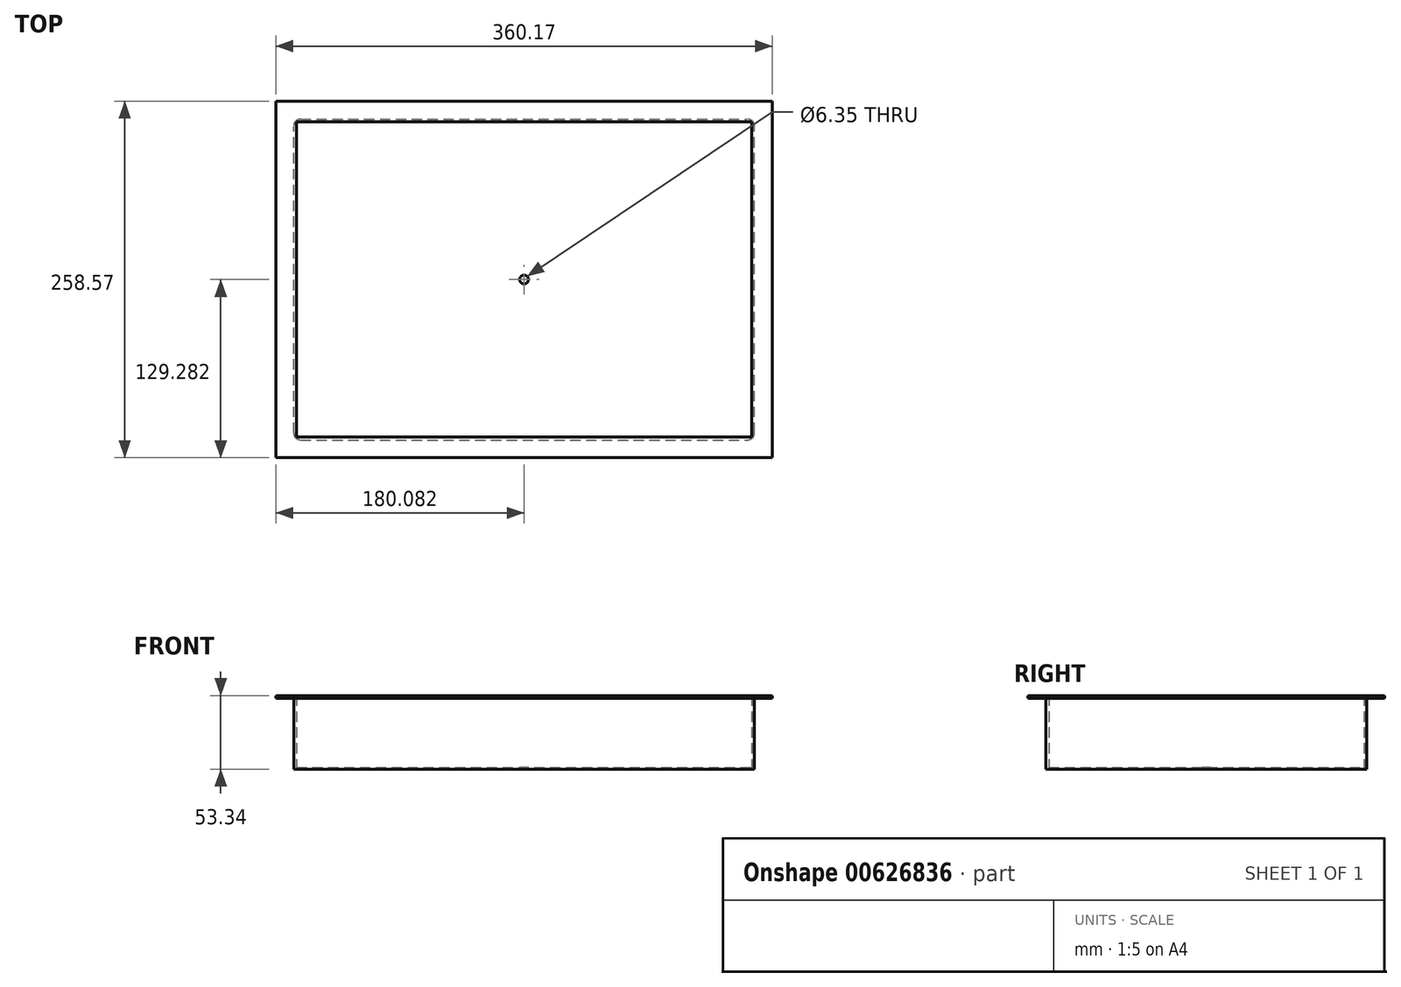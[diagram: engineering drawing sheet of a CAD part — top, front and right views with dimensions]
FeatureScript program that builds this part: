
annotation { "Feature Type Name" : "Feature", "Feature Type Description" : "" }
export const myFeature = defineFeature(function(context is Context, id is Id, definition is map)
    precondition{}
    {
        {
            var Q0;
            Q0=qCreatedBy(makeId("Top.planeOp"),FACE);
            var sketch = newSketch(context, id + "F0", { "sketchPlane" : qUnion([Q0])});
            skLineSegment(sketch, "E0.bottom", {"start": v(0, 0) * mm, "end": v(334.26, 0) * mm});
            skLineSegment(sketch, "E0.top", {"start": v(0, 232.66) * mm, "end": v(334.26, 232.66) * mm});
            skLineSegment(sketch, "E0.left", {"start": v(0, 0) * mm, "end": v(0, 232.66) * mm});
            skLineSegment(sketch, "E0.right", {"start": v(334.26, 0) * mm, "end": v(334.26, 232.66) * mm});
            skLineSegment(sketch, "E1.bottom", {"start": v(2.03, 2.03) * mm, "end": v(332.23, 2.03) * mm});
            skLineSegment(sketch, "E1.top", {"start": v(2.03, 230.63) * mm, "end": v(332.23, 230.63) * mm});
            skLineSegment(sketch, "E1.left", {"start": v(2.03, 2.03) * mm, "end": v(2.03, 230.63) * mm});
            skLineSegment(sketch, "E1.right", {"start": v(332.23, 2.03) * mm, "end": v(332.23, 230.63) * mm});
            skSolve(sketch);
        }
        {
            var Q0;
            Q0 = qSketchRegion(id + "F0", true);
            extrude(context, id + "F1", {"entities" : qUnion([Q0]), "depth" : 53.34 * mm, "offsetDistance" : 25.4 * mm});
        }
        {
            var Q0;
            Q0=makeQuery(id+"F0.imprint","IMPRINT",FACE,{"disambiguationData":[TD([[makeQuery(id+"F0.imprint","IMPRINT",EDGE,{"derivedFrom":sQuery(id+"F0.wireOp",EDGE,"E1.bottom")}),1.0]])]});
            extrude(context, id + "F2", {"entities" : qUnion([Q0]), "operationType" : NewBodyOperationType.ADD, "depth" : 1.27 * mm, "offsetDistance" : 25.4 * mm});
        }
        {
            var Q0;
            Q0=makeQuery(id+"F1.opExtrude","CAP_FACE",FACE,{"disambiguationData":[OSD([sQuery(id+"F0.wireOp",EDGE,"E0.bottom"),sQuery(id+"F0.wireOp",EDGE,"E0.top"),sQuery(id+"F0.wireOp",EDGE,"E0.left"),sQuery(id+"F0.wireOp",EDGE,"E0.right"),sQuery(id+"F0.wireOp",EDGE,"E1.bottom"),sQuery(id+"F0.wireOp",EDGE,"E1.top"),sQuery(id+"F0.wireOp",EDGE,"E1.left"),sQuery(id+"F0.wireOp",EDGE,"E1.right")])],"isStart":false});
            var sketch = newSketch(context, id + "F3", { "sketchPlane" : qUnion([Q0])});
            skLineSegment(sketch, "E2.0", {"start": v(0, 232.66) * mm, "end": v(334.26, 232.66) * mm});
            skLineSegment(sketch, "E3.0", {"start": v(0, 0) * mm, "end": v(0, 232.66) * mm});
            skLineSegment(sketch, "E4.0", {"start": v(0, 0) * mm, "end": v(334.26, 0) * mm});
            skLineSegment(sketch, "E5.0", {"start": v(334.26, 0) * mm, "end": v(334.26, 232.66) * mm});
            skLineSegment(sketch, "E6.0", {"start": v(-12.95, 245.62) * mm, "end": v(347.22, 245.62) * mm});
            skLineSegment(sketch, "E6.1", {"start": v(-12.95, -12.95) * mm, "end": v(-12.95, 245.62) * mm});
            skLineSegment(sketch, "E6.2", {"start": v(-12.95, -12.95) * mm, "end": v(347.22, -12.95) * mm});
            skLineSegment(sketch, "E6.3", {"start": v(347.22, -12.95) * mm, "end": v(347.22, 245.62) * mm});
            skSolve(sketch);
        }
        {
            var Q0;
            Q0=makeQuery(id+"F3.imprint","IMPRINT",FACE,{"disambiguationData":[TD([[makeQuery(id+"F3.imprint","IMPRINT",EDGE,{"derivedFrom":sQuery(id+"F3.wireOp",EDGE,"E2.0")}),1.0]])]});
            extrude(context, id + "F4", {"entities" : qUnion([Q0]), "operationType" : NewBodyOperationType.ADD, "oppositeDirection" : true, "depth" : 2.03 * mm, "offsetDistance" : 25.4 * mm});
        }
        {
            var Q0;
            Q0=makeQuery(id+"F1.opExtrude","SWEPT_EDGE",EDGE,{"disambiguationData":[OSD([sQuery(id+"F0.wireOp",EDGE,"E0.bottom"),sQuery(id+"F0.wireOp",EDGE,"E0.right")])]});
            var Q1;
            Q1=makeQuery(id+"F1.opExtrude","SWEPT_EDGE",EDGE,{"disambiguationData":[OSD([sQuery(id+"F0.wireOp",EDGE,"E0.top"),sQuery(id+"F0.wireOp",EDGE,"E0.right")])]});
            var Q2;
            Q2=makeQuery(id+"F1.opExtrude","SWEPT_EDGE",EDGE,{"disambiguationData":[OSD([sQuery(id+"F0.wireOp",EDGE,"E0.top"),sQuery(id+"F0.wireOp",EDGE,"E0.left")])]});
            var Q3;
            Q3=makeQuery(id+"F1.opExtrude","SWEPT_EDGE",EDGE,{"disambiguationData":[OSD([sQuery(id+"F0.wireOp",EDGE,"E0.bottom"),sQuery(id+"F0.wireOp",EDGE,"E0.left")])]});
            fillet(context, id + "F5", {"entities" : qUnion([Q0, Q1, Q2, Q3]), "radius" : 5.08 * mm, "tangentPropagation" : true, "allowEdgeOverflow" : false});
        }
        {
            var Q0;
            Q0=makeQuery(id+"F2.opExtrude","CAP_FACE",FACE,{"disambiguationData":[OSD([sQuery(id+"F0.wireOp",EDGE,"E1.bottom"),sQuery(id+"F0.wireOp",EDGE,"E1.top"),sQuery(id+"F0.wireOp",EDGE,"E1.left"),sQuery(id+"F0.wireOp",EDGE,"E1.right")])],"isStart":false});
            var sketch = newSketch(context, id + "F6", { "sketchPlane" : qUnion([Q0])});
            skCircle(sketch, "E7", {"center": v(167.13, 116.33) * mm, "radius": 3.18 * mm});
            skLineSegment(sketch, "E8.0.0", {"start": v(332.23, 230.63) * mm, "end": v(2.03, 230.63) * mm});
            skLineSegment(sketch, "E8.0.1", {"start": v(2.03, 230.63) * mm, "end": v(2.03, 2.03) * mm});
            skLineSegment(sketch, "E8.0.2", {"start": v(2.03, 2.03) * mm, "end": v(332.23, 2.03) * mm});
            skLineSegment(sketch, "E8.0.3", {"start": v(332.23, 2.03) * mm, "end": v(332.23, 230.63) * mm});
            skLineSegment(sketch, "E9", {"start": v(2.03, 116.33) * mm, "end": v(332.23, 116.33) * mm, "construction": true});
            skLineSegment(sketch, "E10", {"start": v(167.13, 2.03) * mm, "end": v(167.13, 230.63) * mm, "construction": true});
            skSolve(sketch);
        }
        {
            var Q0;
            Q0=makeQuery(id+"F6.imprint","IMPRINT",FACE,{"disambiguationData":[TD([[makeQuery(id+"F6.imprint","IMPRINT",EDGE,{"derivedFrom":sQuery(id+"F6.wireOp",EDGE,"E7")}),1.0]])]});
            extrude(context, id + "F7", {"entities" : qUnion([Q0]), "operationType" : NewBodyOperationType.REMOVE, "endBound" : BoundingType.THROUGH_ALL, "oppositeDirection" : true, "depth" : 25.4 * mm, "offsetDistance" : 25.4 * mm});
        }
    });
